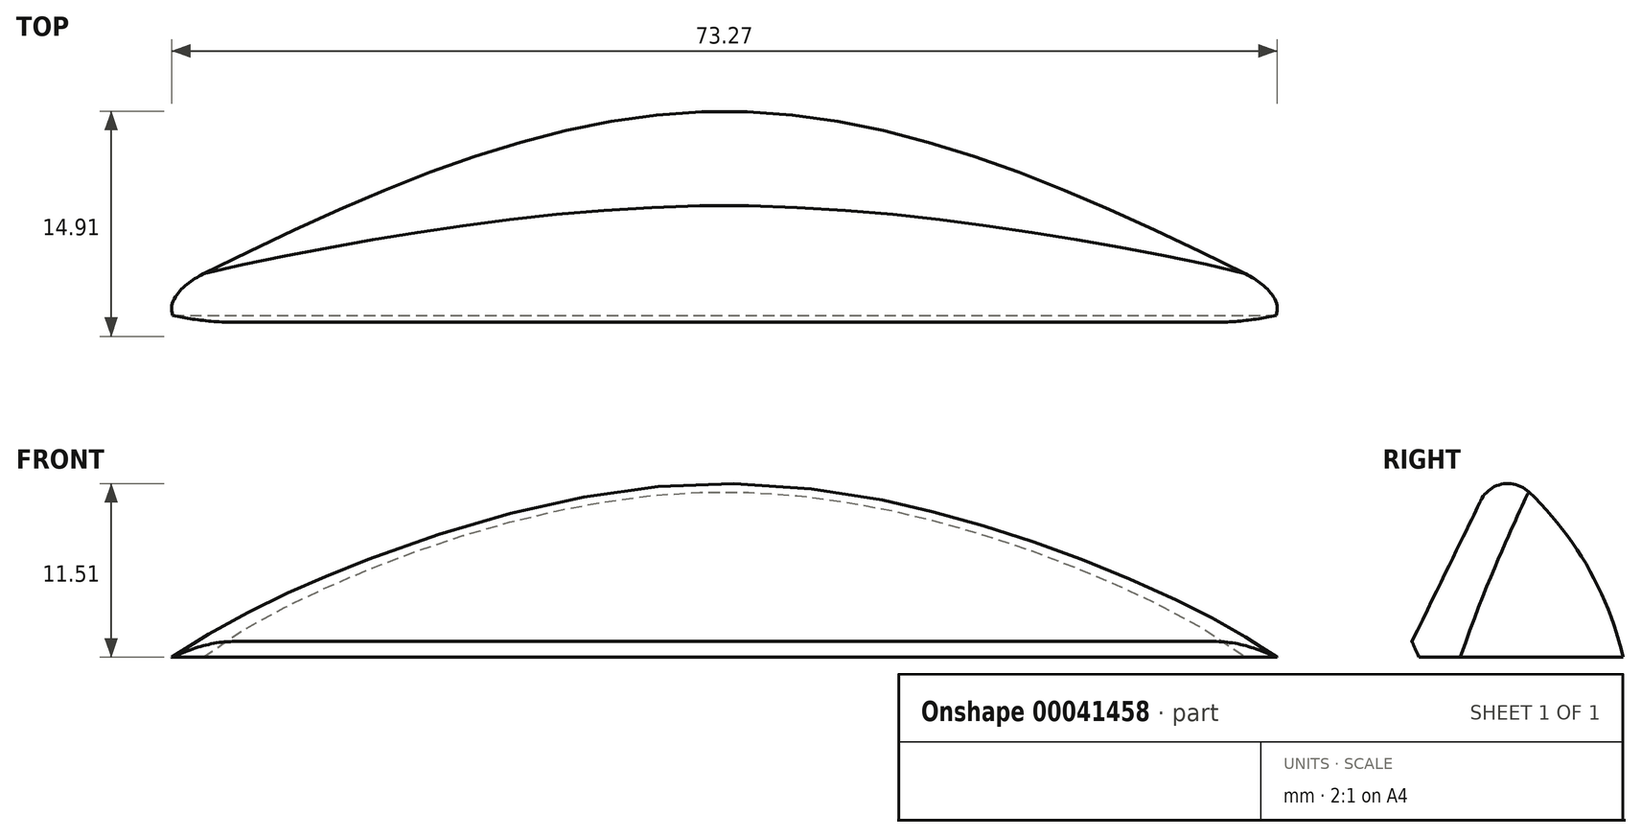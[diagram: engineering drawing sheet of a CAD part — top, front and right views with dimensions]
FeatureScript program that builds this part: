
annotation { "Feature Type Name" : "Feature", "Feature Type Description" : "" }
export const myFeature = defineFeature(function(context is Context, id is Id, definition is map)
    precondition{}
    {
        {
            var Q0;
            Q0=qCreatedBy(makeId("Right.planeOp"),FACE);
            cPlane(context, id + "F0", {"entities" : qUnion([Q0]), "cplaneType" : CPlaneType.OFFSET, "offset" : 40 * mm, "width" : 150 * mm, "height" : 150 * mm});
        }
        {
            var Q0;
            Q0=qCreatedBy(id+"F0.planeOp",FACE);
            cPlane(context, id + "F1", {"entities" : qUnion([Q0]), "cplaneType" : CPlaneType.OFFSET, "offset" : 40 * mm, "width" : 150 * mm, "height" : 150 * mm});
        }
        {
            var Q0;
            Q0=qCreatedBy(id+"F1.planeOp",FACE);
            var sketch = newSketch(context, id + "F2", { "sketchPlane" : qUnion([Q0])});
            skLineSegment(sketch, "E0", {"start": v(0, 0) * mm, "end": v(0, 2.18) * mm});
            skLineSegment(sketch, "E1", {"start": v(0, 2.18) * mm, "end": v(0.96, 0) * mm});
            skLineSegment(sketch, "E2", {"start": v(0.96, 0) * mm, "end": v(0, 0) * mm});
            skSolve(sketch);
        }
        {
            var Q0;
            Q0=qCreatedBy(id+"F0.planeOp",FACE);
            var sketch = newSketch(context, id + "F3", { "sketchPlane" : qUnion([Q0])});
            skLineSegment(sketch, "E3", {"start": v(0, 0) * mm, "end": v(0, 15.86) * mm});
            skArc(sketch, "E4", {"start": v(14.49, 0) * mm, "mid": v(9.34, 9.84) * mm, "end": v(0, 15.86) * mm});
            skLineSegment(sketch, "E5", {"start": v(14.49, 0) * mm, "end": v(0, 0) * mm});
            skSolve(sketch);
        }
        {
            var Q0;
            Q0=qCreatedBy(makeId("Right.planeOp"),FACE);
            var sketch = newSketch(context, id + "F4", { "sketchPlane" : qUnion([Q0])});
            skLineSegment(sketch, "E6", {"start": v(0, 0) * mm, "end": v(0, 2.14) * mm});
            skLineSegment(sketch, "E7", {"start": v(0, 2.14) * mm, "end": v(0.95, 0) * mm});
            skLineSegment(sketch, "E8", {"start": v(0.95, 0) * mm, "end": v(0, 0) * mm});
            skSolve(sketch);
        }
        {
            var Q0;
            Q0 = qSketchRegion(id + "F4", true);
            var Q1;
            Q1=makeQuery(id+"F3.imprint","IMPRINT",FACE,{"disambiguationData":[TD([[makeQuery(id+"F3.imprint","IMPRINT",EDGE,{"derivedFrom":sQuery(id+"F3.wireOp",EDGE,"E3")}),-1.0]])]});
            var Q2;
            Q2 = qSketchRegion(id + "F2", true);
            loft(context, id + "F5", {"sheetProfilesArray" : [{ "sheetProfileEntities" : qUnion([Q0]) }, { "sheetProfileEntities" : qUnion([Q1]) }, { "sheetProfileEntities" : qUnion([Q2]) }]});
        }
        {
            var Q0;
            Q0=makeQuery(id+"F5.opLoft","CAP_FACE",FACE,{"disambiguationData":[OSD([makeQuery(id+"F2.imprint","IMPRINT",FACE,{"disambiguationData":[TD([[makeQuery(id+"F2.imprint","IMPRINT",EDGE,{"derivedFrom":sQuery(id+"F2.wireOp",EDGE,"E0")}),-1.0]])]})])],"isStart":true});
            var sketch = newSketch(context, id + "F6", { "sketchPlane" : qUnion([Q0])});
            skSolve(sketch);
        }
        {
            var Q0;
            {var subQ0=sQuery(id+"F2.wireOp",EDGE,"E0");var subQ1=sQuery(id+"F2.wireOp",EDGE,"E1");var subQ2=sQuery(id+"F2.wireOp",EDGE,"E2");var subQ3=makeQuery(id+"F2.imprint","INTERSECT",VERTEX,{"derivedFrom":[subQ0,subQ1]});var subQ5=makeQuery(id+"F2.imprint","INTERSECT",VERTEX,{"derivedFrom":[subQ0,subQ2]});Q0=makeQuery(id+"F6.imprint","IMPRINT",FACE,{"disambiguationData":[TD([[makeQuery(id+"F6.imprint","IMPRINT",EDGE,{"derivedFrom":makeQuery(id+"F5.opLoft","MID_CAP_EDGE",EDGE,{"disambiguationData":[OSD([subQ0,subQ1,subQ2]),TDD([subQ5,subQ3,makeQuery(id+"F2.imprint","IMPRINT",EDGE,{"derivedFrom":subQ0})])],"capPos":2.0})}),1.0]])]});}
            var sketch = newSketch(context, id + "F7", { "sketchPlane" : qUnion([Q0])});
            skLineSegment(sketch, "E9", {"start": v(0, 0) * mm, "end": v(0, 17.15) * mm});
            skLineSegment(sketch, "E10", {"start": v(0, 17.15) * mm, "end": v(8.37, 17.15) * mm});
            skLineSegment(sketch, "E11", {"start": v(8.37, 17.15) * mm, "end": v(0, 0) * mm});
            skSolve(sketch);
        }
        {
            var Q0;
            {var subQ8=sQuery(id+"F7.wireOp",EDGE,"E10");Q0=makeQuery(id+"F7.imprint","IMPRINT",FACE,{"disambiguationData":[TD([[makeQuery(id+"F7.imprint","IMPRINT",EDGE,{"derivedFrom":subQ8}),-1.0]])]});}
            var Q1;
            {var subQ0=sQuery(id+"F2.wireOp",EDGE,"E0");var subQ1=sQuery(id+"F2.wireOp",EDGE,"E1");var subQ2=sQuery(id+"F2.wireOp",EDGE,"E2");var subQ3=makeQuery(id+"F2.imprint","INTERSECT",VERTEX,{"derivedFrom":[subQ0,subQ1]});var subQ5=makeQuery(id+"F2.imprint","INTERSECT",VERTEX,{"derivedFrom":[subQ0,subQ2]});Q1=makeQuery(id+"F6.imprint","IMPRINT",FACE,{"disambiguationData":[TD([[makeQuery(id+"F6.imprint","IMPRINT",EDGE,{"derivedFrom":makeQuery(id+"F5.opLoft","MID_CAP_EDGE",EDGE,{"disambiguationData":[OSD([subQ0,subQ1,subQ2]),TDD([subQ5,subQ3,makeQuery(id+"F2.imprint","IMPRINT",EDGE,{"derivedFrom":subQ0})])],"capPos":2.0})}),1.0]])]});}
            extrude(context, id + "F8", {"entities" : qUnion([Q0, Q1]), "operationType" : NewBodyOperationType.REMOVE, "endBound" : BoundingType.THROUGH_ALL, "oppositeDirection" : true, "depth" : 25 * mm});
        }
        {
            var Q0;
            {var subQ0=sQuery(id+"F3.wireOp",EDGE,"E3");var subQ1=sQuery(id+"F3.wireOp",EDGE,"E4");var subQ2=sQuery(id+"F3.wireOp",EDGE,"E5");var subQ3=sQuery(id+"F4.wireOp",EDGE,"E6");var subQ4=sQuery(id+"F4.wireOp",EDGE,"E7");var subQ5=sQuery(id+"F4.wireOp",EDGE,"E8");Q0=makeQuery(id+"F8.boolean.opBoolean","INTERSECT",EDGE,{"derivedFrom":[makeQuery(id+"F5.opLoft","SWEPT_FACE",FACE,{"disambiguationData":[OSD([subQ0,subQ1,subQ2,subQ3,subQ4,subQ5]),TDD([makeQuery(id+"F3.imprint","INTERSECT",VERTEX,{"derivedFrom":[subQ0,subQ1]}),makeQuery(id+"F3.imprint","INTERSECT",VERTEX,{"derivedFrom":[subQ1,subQ2]}),makeQuery(id+"F3.imprint","IMPRINT",EDGE,{"derivedFrom":subQ1}),makeQuery(id+"F4.imprint","INTERSECT",VERTEX,{"derivedFrom":[subQ3,subQ4]}),makeQuery(id+"F4.imprint","INTERSECT",VERTEX,{"derivedFrom":[subQ4,subQ5]}),makeQuery(id+"F4.imprint","IMPRINT",EDGE,{"derivedFrom":subQ4})])]}),makeQuery(id+"F8.opExtrude","SWEPT_FACE",FACE,{"disambiguationData":[OSD([sQuery(id+"F7.wireOp",EDGE,"E11")])]})]});}
            fillet(context, id + "F9", {"entities" : qUnion([Q0]), "radius" : 2 * mm, "tangentPropagation" : true, "allowEdgeOverflow" : false});
        }
    });
